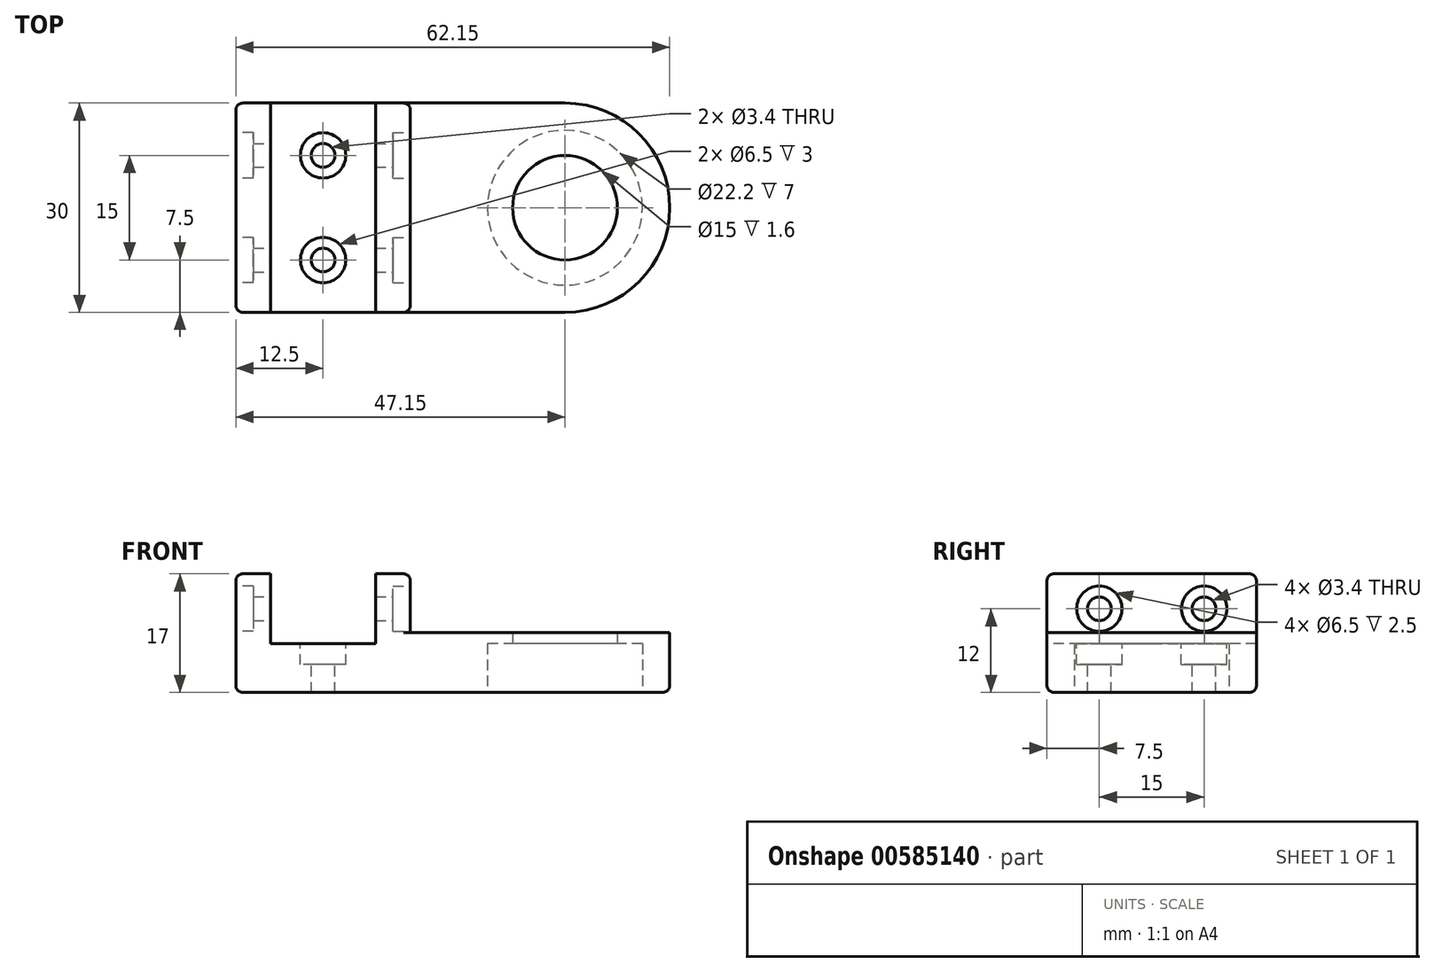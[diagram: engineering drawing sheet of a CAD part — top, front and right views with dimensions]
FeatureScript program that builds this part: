
annotation { "Feature Type Name" : "Feature", "Feature Type Description" : "" }
export const myFeature = defineFeature(function(context is Context, id is Id, definition is map)
    precondition{}
    {
        {
            var Q0;
            Q0=qCreatedBy(makeId("Top.planeOp"),FACE);
            var sketch = newSketch(context, id + "F0", { "sketchPlane" : qUnion([Q0])});
            skCircle(sketch, "E0", {"center": v(0, 0) * mm, "radius": 4 * mm, "construction": true});
            skCircle(sketch, "E1", {"center": v(0, 0) * mm, "radius": 11.1 * mm});
            skArc(sketch, "E2", {"start": v(0, -15) * mm, "mid": v(15, 0) * mm, "end": v(0, 15) * mm});
            skLineSegment(sketch, "E3", {"start": v(0, 15) * mm, "end": v(-47.15, 15) * mm});
            skLineSegment(sketch, "E4", {"start": v(0, -15) * mm, "end": v(-47.15, -15) * mm});
            skLineSegment(sketch, "E5", {"start": v(-47.15, 15) * mm, "end": v(-47.15, -15) * mm});
            skSolve(sketch);
        }
        {
            var Q0;
            Q0=qSketchRegion(id+"F0",true);
            extrude(context, id + "F1", {"entities" : qUnion([Q0]), "depth" : 7 * mm});
        }
        {
            var Q0;
            Q0=makeQuery(id+"F1.opExtrude","CAP_FACE",FACE,{"disambiguationData":[OSD([sQuery(id+"F0.wireOp",EDGE,"E1"),sQuery(id+"F0.wireOp",EDGE,"E2"),sQuery(id+"F0.wireOp",EDGE,"E3"),sQuery(id+"F0.wireOp",EDGE,"E4"),sQuery(id+"F0.wireOp",EDGE,"E5")])],"isStart":false});
            var sketch = newSketch(context, id + "F2", { "sketchPlane" : qUnion([Q0])});
            skLineSegment(sketch, "E6.bottom", {"start": v(-47.15, 15) * mm, "end": v(-42.15, 15) * mm});
            skLineSegment(sketch, "E6.top", {"start": v(-47.15, -15) * mm, "end": v(-42.15, -15) * mm});
            skLineSegment(sketch, "E6.left", {"start": v(-47.15, 15) * mm, "end": v(-47.15, -15) * mm});
            skLineSegment(sketch, "E6.right", {"start": v(-42.15, 15) * mm, "end": v(-42.15, -15) * mm});
            skLineSegment(sketch, "E7.bottom", {"start": v(-27.15, 15) * mm, "end": v(-22.15, 15) * mm});
            skLineSegment(sketch, "E7.top", {"start": v(-27.15, -15) * mm, "end": v(-22.15, -15) * mm});
            skLineSegment(sketch, "E7.left", {"start": v(-27.15, 15) * mm, "end": v(-27.15, -15) * mm});
            skLineSegment(sketch, "E7.right", {"start": v(-22.15, 15) * mm, "end": v(-22.15, -15) * mm});
            skSolve(sketch);
        }
        {
            var Q0;
            Q0=qSketchRegion(id+"F2",true);
            extrude(context, id + "F3", {"entities" : qUnion([Q0]), "operationType" : NewBodyOperationType.ADD, "depth" : 10 * mm});
        }
        {
            var Q0;
            Q0=makeQuery(id+"F3.opExtrude","SWEPT_FACE",FACE,{"disambiguationData":[OSD([sQuery(id+"F2.wireOp",EDGE,"E6.right")])]});
            var sketch = newSketch(context, id + "F4", { "sketchPlane" : qUnion([Q0])});
            skCircle(sketch, "E8", {"center": v(7.5, 12) * mm, "radius": 1.7 * mm});
            skPoint(sketch, "E8.centerSnap0", {"position": v(15, 12) * mm});
            skCircle(sketch, "E9", {"center": v(-7.5, 12) * mm, "radius": 1.7 * mm});
            skPoint(sketch, "E9.centerSnap0", {"position": v(-15, 12) * mm});
            skSolve(sketch);
        }
        {
            var Q0;
            Q0=qSketchRegion(id+"F4",true);
            extrude(context, id + "F5", {"entities" : qUnion([Q0]), "operationType" : NewBodyOperationType.REMOVE, "endBound" : BoundingType.THROUGH_ALL, "oppositeDirection" : true, "depth" : 25 * mm});
        }
        {
            var Q0;
            Q0=makeQuery(id+"F3.boolean.opBoolean","MERGE",FACE,{"derivedFrom":[makeQuery(id+"F1.opExtrude","SWEPT_FACE",FACE,{"disambiguationData":[OSD([sQuery(id+"F0.wireOp",EDGE,"E5")])]}),makeQuery(id+"F3.opExtrude","SWEPT_FACE",FACE,{"disambiguationData":[OSD([sQuery(id+"F2.wireOp",EDGE,"E6.left")])]})]});
            var sketch = newSketch(context, id + "F6", { "sketchPlane" : qUnion([Q0])});
            skCircle(sketch, "E10", {"center": v(-7.5, 12) * mm, "radius": 3.25 * mm});
            skCircle(sketch, "E11", {"center": v(7.5, 12) * mm, "radius": 3.25 * mm});
            skSolve(sketch);
        }
        {
            var Q0;
            Q0=qSketchRegion(id+"F6",true);
            extrude(context, id + "F7", {"entities" : qUnion([Q0]), "operationType" : NewBodyOperationType.REMOVE, "oppositeDirection" : true, "depth" : 2.5 * mm});
        }
        {
            var Q0;
            Q0=makeQuery(id+"F3.opExtrude","SWEPT_FACE",FACE,{"disambiguationData":[OSD([sQuery(id+"F2.wireOp",EDGE,"E7.right")])]});
            var sketch = newSketch(context, id + "F8", { "sketchPlane" : qUnion([Q0])});
            skCircle(sketch, "E12", {"center": v(7.5, 12) * mm, "radius": 1.7 * mm});
            skPoint(sketch, "E12.centerSnap0", {"position": v(15, 12) * mm});
            skCircle(sketch, "E13", {"center": v(-7.5, 12) * mm, "radius": 1.7 * mm});
            skPoint(sketch, "E13.centerSnap0", {"position": v(-15, 12) * mm});
            skSolve(sketch);
        }
        {
            var Q0;
            Q0=qSketchRegion(id+"F8",true);
            extrude(context, id + "F9", {"entities" : qUnion([Q0]), "operationType" : NewBodyOperationType.REMOVE, "endBound" : BoundingType.THROUGH_ALL, "oppositeDirection" : true, "depth" : 25 * mm});
        }
        {
            var Q0;
            Q0=makeQuery(id+"F3.opExtrude","SWEPT_FACE",FACE,{"disambiguationData":[OSD([sQuery(id+"F2.wireOp",EDGE,"E7.right")])]});
            var sketch = newSketch(context, id + "F10", { "sketchPlane" : qUnion([Q0])});
            skCircle(sketch, "E14", {"center": v(7.5, 12) * mm, "radius": 3.25 * mm});
            skCircle(sketch, "E15", {"center": v(-7.5, 12) * mm, "radius": 3.25 * mm});
            skSolve(sketch);
        }
        {
            var Q0;
            Q0=qSketchRegion(id+"F10",true);
            extrude(context, id + "F11", {"entities" : qUnion([Q0]), "operationType" : NewBodyOperationType.REMOVE, "oppositeDirection" : true, "depth" : 2.5 * mm});
        }
        {
            var Q0;
            {var subQ0=sQuery(id+"F0.wireOp",EDGE,"E4");var subQ1=sQuery(id+"F0.wireOp",EDGE,"E3");var subQ2=sQuery(id+"F0.wireOp",EDGE,"E2");var subQ3=sQuery(id+"F0.wireOp",EDGE,"E1");Q0=makeQuery(id+"F3.boolean.opBoolean","SPLIT",FACE,{"disambiguationData":[TD([makeQuery(id+"F1.opExtrude","SWEPT_FACE",FACE,{"disambiguationData":[OSD([subQ3])]})])],"derivedFrom":makeQuery(id+"F1.opExtrude","CAP_FACE",FACE,{"disambiguationData":[OSD([subQ3,subQ2,subQ1,subQ0,sQuery(id+"F0.wireOp",EDGE,"E5")])],"isStart":false})});}
            var sketch = newSketch(context, id + "F12", { "sketchPlane" : qUnion([Q0])});
            skLineSegment(sketch, "E16.0", {"start": v(0, 15) * mm, "end": v(-22.15, 15) * mm});
            skLineSegment(sketch, "E17.0", {"start": v(0, -15) * mm, "end": v(-22.15, -15) * mm});
            skArc(sketch, "E18.0", {"start": v(0, -15) * mm, "mid": v(15, 0) * mm, "end": v(0, 15) * mm});
            skLineSegment(sketch, "E19.0", {"start": v(-22.15, 15) * mm, "end": v(-22.15, -15) * mm});
            skCircle(sketch, "E20", {"center": v(0, 0) * mm, "radius": 7.5 * mm});
            skSolve(sketch);
        }
        {
            var Q0;
            Q0=qSketchRegion(id+"F12",true);
            extrude(context, id + "F13", {"entities" : qUnion([Q0]), "operationType" : NewBodyOperationType.ADD, "depth" : 1.6 * mm});
        }
        {
            var Q0;
            Q0=makeQuery(id+"F1.opExtrude","CAP_EDGE",EDGE,{"disambiguationData":[OSD([sQuery(id+"F0.wireOp",EDGE,"E5")])],"isStart":true});
            var Q1;
            Q1=makeQuery(id+"F1.opExtrude","CAP_EDGE",EDGE,{"disambiguationData":[OSD([sQuery(id+"F0.wireOp",EDGE,"E4")])],"isStart":true});
            var Q2;
            Q2=makeQuery(id+"F1.opExtrude","CAP_EDGE",EDGE,{"disambiguationData":[OSD([sQuery(id+"F0.wireOp",EDGE,"E2")])],"isStart":true});
            var Q3;
            Q3=makeQuery(id+"F1.opExtrude","CAP_EDGE",EDGE,{"disambiguationData":[OSD([sQuery(id+"F0.wireOp",EDGE,"E3")])],"isStart":true});
            var Q4;
            Q4=makeQuery(id+"F3.boolean.opBoolean","MERGE",EDGE,{"derivedFrom":[makeQuery(id+"F1.opExtrude","SWEPT_EDGE",EDGE,{"disambiguationData":[OSD([sQuery(id+"F0.wireOp",EDGE,"E4"),sQuery(id+"F0.wireOp",EDGE,"E5")])]}),makeQuery(id+"F3.opExtrude","SWEPT_EDGE",EDGE,{"disambiguationData":[OSD([sQuery(id+"F2.wireOp",EDGE,"E6.top"),sQuery(id+"F2.wireOp",EDGE,"E6.left")])]})]});
            var Q5;
            Q5=makeQuery(id+"F3.boolean.opBoolean","MERGE",EDGE,{"derivedFrom":[makeQuery(id+"F1.opExtrude","SWEPT_EDGE",EDGE,{"disambiguationData":[OSD([sQuery(id+"F0.wireOp",EDGE,"E3"),sQuery(id+"F0.wireOp",EDGE,"E5")])]}),makeQuery(id+"F3.opExtrude","SWEPT_EDGE",EDGE,{"disambiguationData":[OSD([sQuery(id+"F2.wireOp",EDGE,"E6.bottom"),sQuery(id+"F2.wireOp",EDGE,"E6.left")])]})]});
            var Q6;
            Q6=makeQuery(id+"F3.opExtrude","CAP_EDGE",EDGE,{"disambiguationData":[OSD([sQuery(id+"F2.wireOp",EDGE,"E6.left")])],"isStart":false});
            var Q7;
            Q7=makeQuery(id+"F3.opExtrude","CAP_EDGE",EDGE,{"disambiguationData":[OSD([sQuery(id+"F2.wireOp",EDGE,"E7.right")])],"isStart":false});
            var Q8;
            Q8=makeQuery(id+"F3.opExtrude","SWEPT_EDGE",EDGE,{"disambiguationData":[OSD([sQuery(id+"F0.wireOp",EDGE,"E4"),sQuery(id+"F2.wireOp",EDGE,"E7.top"),sQuery(id+"F2.wireOp",EDGE,"E7.right")])]});
            var Q9;
            Q9=makeQuery(id+"F3.opExtrude","SWEPT_EDGE",EDGE,{"disambiguationData":[OSD([sQuery(id+"F0.wireOp",EDGE,"E3"),sQuery(id+"F2.wireOp",EDGE,"E7.bottom"),sQuery(id+"F2.wireOp",EDGE,"E7.right")])]});
            fillet(context, id + "F14", {"entities" : qUnion([Q0, Q1, Q2, Q3, Q4, Q5, Q6, Q7, Q8, Q9]), "radius" : 1 * mm, "tangentPropagation" : true, "allowEdgeOverflow" : false});
        }
        {
            var Q0;
            {var subQ0=sQuery(id+"F0.wireOp",EDGE,"E4");var subQ1=sQuery(id+"F0.wireOp",EDGE,"E3");Q0=makeQuery(id+"F3.boolean.opBoolean","SPLIT",FACE,{"disambiguationData":[TD([makeQuery(id+"F3.opExtrude","SWEPT_FACE",FACE,{"disambiguationData":[OSD([sQuery(id+"F2.wireOp",EDGE,"E6.right")])]})])],"derivedFrom":makeQuery(id+"F1.opExtrude","CAP_FACE",FACE,{"disambiguationData":[OSD([sQuery(id+"F0.wireOp",EDGE,"E1"),sQuery(id+"F0.wireOp",EDGE,"E2"),subQ1,subQ0,sQuery(id+"F0.wireOp",EDGE,"E5")])],"isStart":false})});}
            var sketch = newSketch(context, id + "F15", { "sketchPlane" : qUnion([Q0])});
            skCircle(sketch, "E21", {"center": v(-34.65, -7.5) * mm, "radius": 1.7 * mm});
            skPoint(sketch, "E21.centerSnap0", {"position": v(-34.65, -15) * mm});
            skCircle(sketch, "E22", {"center": v(-34.65, 7.5) * mm, "radius": 1.7 * mm});
            skPoint(sketch, "E22.centerSnap0", {"position": v(-34.65, 15) * mm});
            skSolve(sketch);
        }
        {
            var Q0;
            Q0=qSketchRegion(id+"F15",true);
            extrude(context, id + "F16", {"entities" : qUnion([Q0]), "operationType" : NewBodyOperationType.REMOVE, "endBound" : BoundingType.THROUGH_ALL, "oppositeDirection" : true, "depth" : 25 * mm});
        }
        {
            var Q0;
            {var subQ0=sQuery(id+"F0.wireOp",EDGE,"E4");var subQ1=sQuery(id+"F0.wireOp",EDGE,"E3");Q0=makeQuery(id+"F3.boolean.opBoolean","SPLIT",FACE,{"disambiguationData":[TD([makeQuery(id+"F3.opExtrude","SWEPT_FACE",FACE,{"disambiguationData":[OSD([sQuery(id+"F2.wireOp",EDGE,"E6.right")])]})])],"derivedFrom":makeQuery(id+"F1.opExtrude","CAP_FACE",FACE,{"disambiguationData":[OSD([sQuery(id+"F0.wireOp",EDGE,"E1"),sQuery(id+"F0.wireOp",EDGE,"E2"),subQ1,subQ0,sQuery(id+"F0.wireOp",EDGE,"E5")])],"isStart":false})});}
            var sketch = newSketch(context, id + "F17", { "sketchPlane" : qUnion([Q0])});
            skCircle(sketch, "E23", {"center": v(-34.65, -7.5) * mm, "radius": 3.25 * mm});
            skCircle(sketch, "E24", {"center": v(-34.65, 7.5) * mm, "radius": 3.25 * mm});
            skSolve(sketch);
        }
        {
            var Q0;
            Q0=qSketchRegion(id+"F17",true);
            extrude(context, id + "F18", {"entities" : qUnion([Q0]), "operationType" : NewBodyOperationType.REMOVE, "oppositeDirection" : true, "depth" : 3 * mm});
        }
        {
            var Q0;
            Q0=makeQuery(id+"F3.opExtrude","CAP_EDGE",EDGE,{"disambiguationData":[OSD([sQuery(id+"F2.wireOp",EDGE,"E6.bottom")])],"isStart":false});
            var Q1;
            Q1=makeQuery(id+"F3.opExtrude","CAP_EDGE",EDGE,{"disambiguationData":[OSD([sQuery(id+"F2.wireOp",EDGE,"E7.bottom")])],"isStart":false});
            var Q2;
            Q2=makeQuery(id+"F3.opExtrude","CAP_EDGE",EDGE,{"disambiguationData":[OSD([sQuery(id+"F2.wireOp",EDGE,"E7.top")])],"isStart":false});
            var Q3;
            Q3=makeQuery(id+"F3.opExtrude","CAP_EDGE",EDGE,{"disambiguationData":[OSD([sQuery(id+"F2.wireOp",EDGE,"E6.top")])],"isStart":false});
            fillet(context, id + "F19", {"entities" : qUnion([Q0, Q1, Q2, Q3]), "radius" : 1 * mm, "tangentPropagation" : true, "allowEdgeOverflow" : false});
        }
    });
